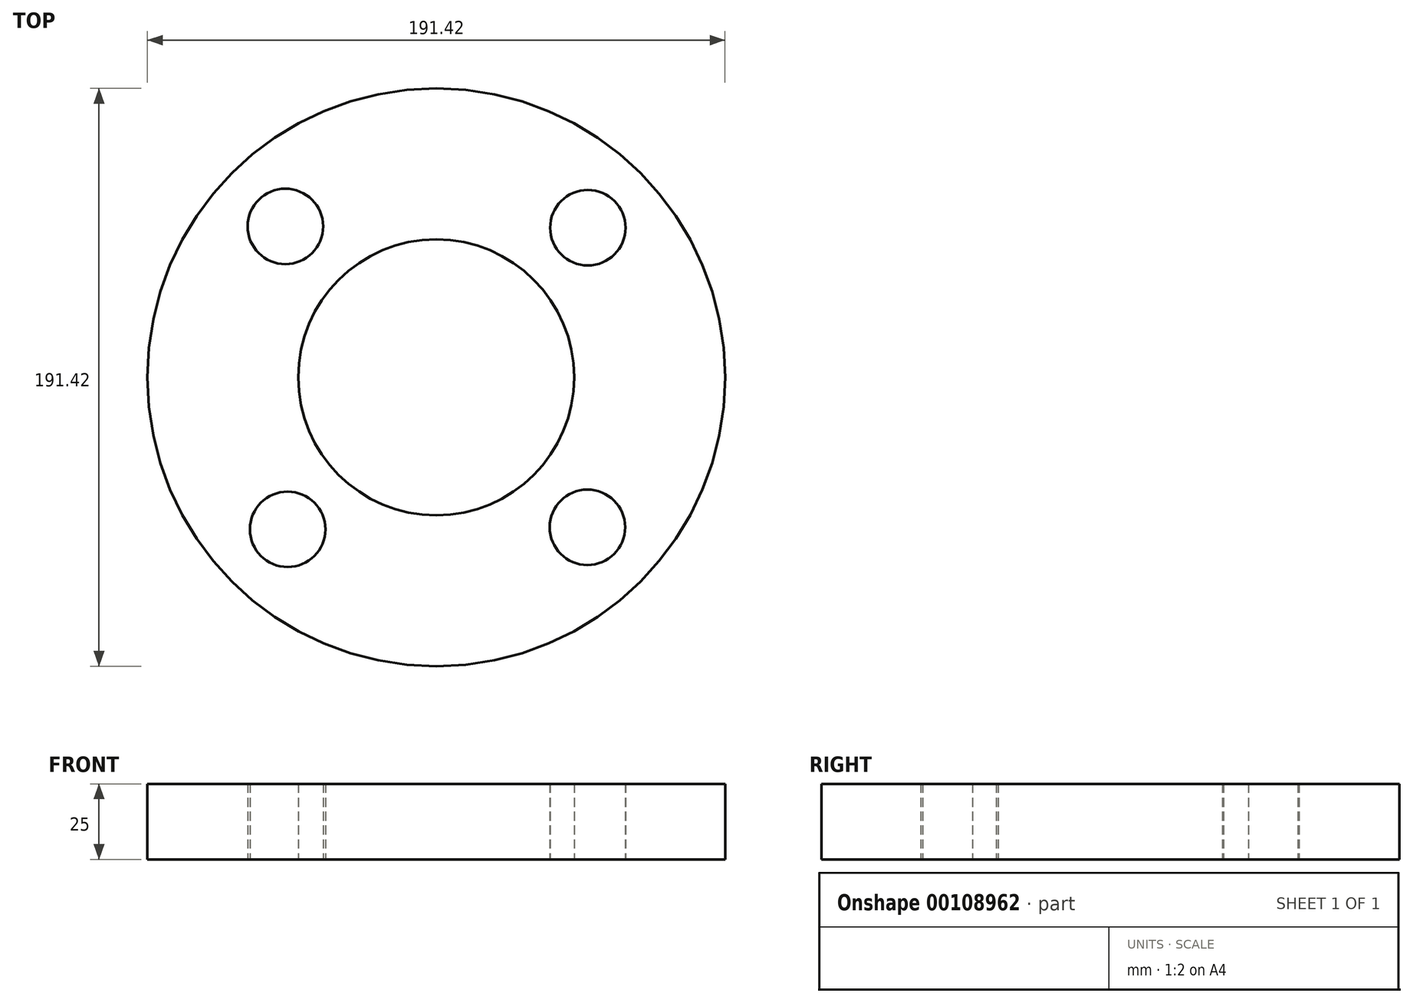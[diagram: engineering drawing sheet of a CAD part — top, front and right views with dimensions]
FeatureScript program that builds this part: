
annotation { "Feature Type Name" : "Feature", "Feature Type Description" : "" }
export const myFeature = defineFeature(function(context is Context, id is Id, definition is map)
    precondition{}
    {
        {
            var Q0;
            Q0=qCreatedBy(makeId("Top.planeOp"),FACE);
            var sketch = newSketch(context, id + "F0", { "sketchPlane" : qUnion([Q0])});
            skLineSegment(sketch, "E0.bottom", {"start": v(50, -50) * mm, "end": v(-50, -50) * mm});
            skLineSegment(sketch, "E0.top", {"start": v(50, 50) * mm, "end": v(-50, 50) * mm});
            skLineSegment(sketch, "E0.left", {"start": v(50, -50) * mm, "end": v(50, 50) * mm});
            skLineSegment(sketch, "E0.right", {"start": v(-50, -50) * mm, "end": v(-50, 50) * mm});
            skPoint(sketch, "E0.middle", {"position": v(0, 0) * mm});
            skCircle(sketch, "E1", {"center": v(-50, 50) * mm, "radius": 12.5 * mm});
            skCircle(sketch, "E2", {"center": v(50.24, 49.58) * mm, "radius": 12.5 * mm});
            skCircle(sketch, "E3", {"center": v(50.08, -49.7) * mm, "radius": 12.5 * mm});
            skCircle(sketch, "E4", {"center": v(-49.25, -50.36) * mm, "radius": 12.5 * mm});
            skCircle(sketch, "E5", {"center": v(0, 0) * mm, "radius": 95.71 * mm});
            skCircle(sketch, "E6", {"center": v(0, 0) * mm, "radius": 45.71 * mm});
            skSolve(sketch);
        }
        {
            var Q0;
            Q0=makeQuery(id+"F0.imprint","IMPRINT",FACE,{"disambiguationData":[TD([[makeQuery(id+"F0.imprint","IMPRINT",EDGE,{"derivedFrom":sQuery(id+"F0.wireOp",EDGE,"E6")}),-1.0]])]});
            var Q1;
            Q1=makeQuery(id+"F0.imprint","IMPRINT",FACE,{"disambiguationData":[TD([[makeQuery(id+"F0.imprint","IMPRINT",EDGE,{"derivedFrom":sQuery(id+"F0.wireOp",EDGE,"E5")}),1.0]])]});
            extrude(context, id + "F1", {"entities" : qUnion([Q0, Q1]), "depth" : 25 * mm});
        }
    });
